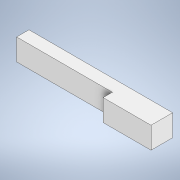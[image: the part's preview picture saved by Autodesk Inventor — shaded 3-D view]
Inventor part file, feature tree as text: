
AUTODESK INVENTOR PART (.ipt)
format: ipt  version: 2021 (Build 250183000, 183)  size: 95,232 bytes
history: native  units: in
note: dims shown in document units (in); Inventor stores cm internally (conversion verified against a paired STEP export)
features: extrude x1, sketch x1
ambient origin geometry x8: Origin, YZ Plane, XZ Plane, XY Plane, X Axis, Y Axis, Z Axis, Center Point
bodies: Solid1 (feature_tree)
feature tree (2):
  extrude  "Extrusion1"  Depth=3.875in
  sketch  "Sketch1"  dims[d0=5.8125in d1=3.875in d2=0.875in d3=0.5in d4=0.875in d5=0.0in]
